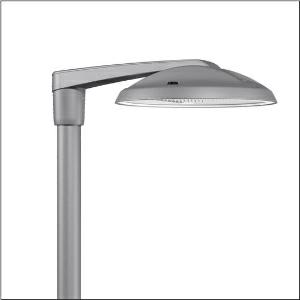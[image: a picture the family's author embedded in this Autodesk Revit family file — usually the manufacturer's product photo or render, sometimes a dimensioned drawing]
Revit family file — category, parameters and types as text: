
# Revit family: dl_r__50_mini___st1_0a_5xa248d33s08me_5901
name_source: partatom
category: Lighting Fixtures
units: mm (PartAtom-declared; Revit-internal decimal feet)

## family parameters
Cut with Voids When Loaded = No
Host = Face
Light Source = No
Part Type = Normal
Room Calculation Point = No
Round Connector Dimension = Use Diameter
Shared = No

## types (1)
- --- (1 x LED, 15380 lm, 110.3 W, 3000K)
    Apparent Load = 110 VA
    CIE Flux Codes = 37 72 97 100 100
    Color Rendering = 70
    Color Temperature = 3000K
    Default Elevation = 1800 mm
    Description = DL® 50 mini, mast luminaire, primary light control with lens, of PMMA, primary optical cover: cover, of toughened safety glass, transparent, light distribution: ST1.0a, light emission: direct distribution, primary light characteristic: asymmetric, installation type: post-top, side-entry, LED, High Power LED, rated luminous flux: 15.380lm, luminous efficacy: 139lm/W, light colour: 730, colour temperature: 3000K, control: overheat protection, constant luminous flux control, time-dependent luminous flux control, flexible luminous flux parameterisation, mains connection: 230..240V, AC, 50/60Hz, connection cable pre-assembled, cable length: 10,5m, start of lifetime: 110W, end of service life: 116W, reduction: 49W, luminaire housing, of diecast aluminium, powder-coated, Siteco® metallic grey (DB 702S), inclination adjustable: 0°, 5°, 10° (post-top) | 0°, -5°, -10°, -15° (side-entry), please order mast post-top element or mast side-entry element separately, diameter: 500mm, height: 115mm, post-top: for spigot size d x l = 76 x 100mm; with reducer (optional accessory) 60 x 100mm | side-entry: for spigot size d x l = 60 x 100mm; with reducer (optional accessory) 42 x 100mm, Smart Interface above, protection rating (complete): IP66, insulation class (complete): insulation class II (safety insulation), certification: CE, ENEC, ENEC+, VDE, impact resistance: IK08, permissible operating ambient temperature for outdoor applications: -25..+40°C, standard-compliant lighting for roads and squares, packaging unit: 1 piece

Light Distribution: ST1.0a
    Height = 115 mm
    Lamp = 1 x LED
    Lamp Light Flux = 15380 lm
    Lamp Power = 110.3 W
    Lamp count = 1
    Length = 500 mm
    Luminous efficacy = 139 lm/W
    Manufacturer = Siteco
    ModVariant = No
    Model = 5XA248D33S08ME
    Number of Poles = 1
    OnlyDefault = Yes
    Power Factor = 1
    Product Name = DL® 50 mini | ST1.0a
    Product group = mast luminaire | pylon top
    ProductGroupID = 6100
    Protection Class = Protection class II
    Protection Degree = IP 66
    RLX_Detail_Level = 1
    RLX_Emergency_Light_Flux = 0 lm
    RLX_Emergency_Type = 0
    RLX_Emergency_Type_DB = No
    RlxData = <blob elided: 106201 chars, md5=0e2c3af6>
    Socket = socket
    Standby Power = 0 W
    System Light Flux = 15380 lm
    System Power = 110 W
    Type Comments = factory setting: luminous flux: 100 % | dim-lin: 254 | 565 mA
    Type Image = l_1251788.jpg
    URL = http://relux.com
    VarID = @adj_033175
    Voltage = 0 V
    Weight = 0.00 kg
    Width = 0 mm  [stored 0 ft]

note: [stored X ft] marks values corroborated as IEEE doubles in the binary element streams (Revit-internal decimal feet)

## geometry (parser evidence)
native form markers: Blend x4, Sweep x9
no freeform markers — native parametric forms only
